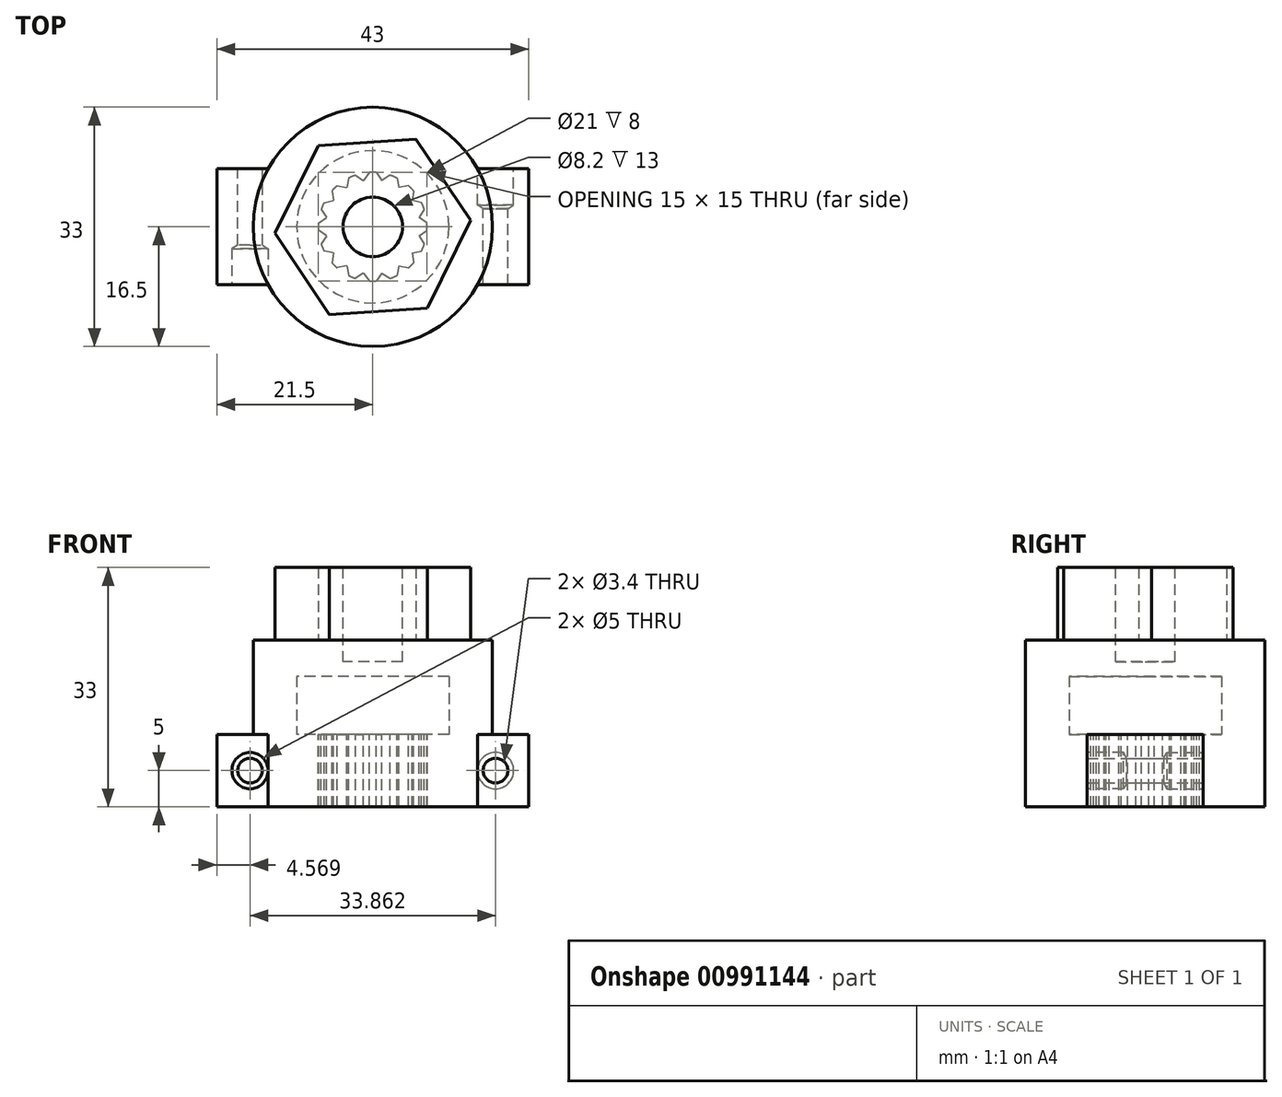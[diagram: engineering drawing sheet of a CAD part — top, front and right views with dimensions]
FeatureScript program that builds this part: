
annotation { "Feature Type Name" : "Feature", "Feature Type Description" : "" }
export const myFeature = defineFeature(function(context is Context, id is Id, definition is map)
    precondition{}
    {
        {
            var Q0;
            Q0=qCreatedBy(makeId("Top.planeOp"),FACE);
            var sketch = newSketch(context, id + "F0", { "sketchPlane" : qUnion([Q0])});
            skLineSegment(sketch, "E0", {"start": v(0, 0) * mm, "end": v(27.34, 0) * mm, "construction": true});
            skLineSegment(sketch, "E1", {"start": v(0, 0) * mm, "end": v(23.28, 9.64) * mm, "construction": true});
            skArc(sketch, "E2", {"start": v(7.5, 0) * mm, "mid": v(7.36, 1.46) * mm, "end": v(6.93, 2.87) * mm});
            skCircle(sketch, "E3", {"center": v(0, 0) * mm, "radius": 10.5 * mm});
            skLineSegment(sketch, "E4", {"start": v(7.5, 0) * mm, "end": v(10.5, 0) * mm});
            skLineSegment(sketch, "E5", {"start": v(10.5, 0) * mm, "end": v(21.5, 0) * mm});
            skLineSegment(sketch, "E6", {"start": v(21.5, 0) * mm, "end": v(21.5, 8) * mm});
            skLineSegment(sketch, "E7", {"start": v(21.5, 8) * mm, "end": v(14.43, 8) * mm});
            skLineSegment(sketch, "E8.MirrorCS", {"start": v(-10.5, 0) * mm, "end": v(-21.5, 0) * mm});
            skLineSegment(sketch, "E9.MirrorCS", {"start": v(-21.5, 0) * mm, "end": v(-21.5, 8) * mm});
            skLineSegment(sketch, "E10.MirrorCS", {"start": v(-21.5, 8) * mm, "end": v(-14.43, 8) * mm});
            skCircle(sketch, "E11", {"center": v(0, 0) * mm, "radius": 16.5 * mm});
            skLineSegment(sketch, "E12.MirrorCS", {"start": v(21.5, 0) * mm, "end": v(21.5, -8) * mm});
            skLineSegment(sketch, "E13.MirrorCS", {"start": v(21.5, -8) * mm, "end": v(14.43, -8) * mm});
            skLineSegment(sketch, "E14.MirrorCS", {"start": v(-21.5, 0) * mm, "end": v(-21.5, -8) * mm});
            skLineSegment(sketch, "E15.MirrorCS", {"start": v(-21.5, -8) * mm, "end": v(-14.43, -8) * mm});
            skLineSegment(sketch, "E16", {"start": v(-10.5, 0) * mm, "end": v(-7.5, 0) * mm});
            skLineSegment(sketch, "E17", {"start": v(7.36, 1.46) * mm, "end": v(0, 0) * mm, "construction": true});
            skLineSegment(sketch, "E18", {"start": v(7.1, 2.4) * mm, "end": v(6.38, 1.27) * mm});
            skLineSegment(sketch, "E19.MirrorCS", {"start": v(7.48, 0.5) * mm, "end": v(6.38, 1.27) * mm});
            skArc(sketch, "E20.1.0", {"start": v(6.93, 2.87) * mm, "mid": v(6.24, 4.17) * mm, "end": v(5.3, 5.3) * mm});
            skLineSegment(sketch, "E20.1.1", {"start": v(6.72, 3.33) * mm, "end": v(5.4, 3.61) * mm});
            skLineSegment(sketch, "E20.1.2", {"start": v(5.64, 4.94) * mm, "end": v(5.4, 3.61) * mm});
            skArc(sketch, "E20.2.0", {"start": v(5.3, 5.3) * mm, "mid": v(4.17, 6.24) * mm, "end": v(2.87, 6.93) * mm});
            skLineSegment(sketch, "E20.2.1", {"start": v(4.94, 5.64) * mm, "end": v(3.61, 5.4) * mm});
            skLineSegment(sketch, "E20.2.2", {"start": v(3.33, 6.72) * mm, "end": v(3.61, 5.4) * mm});
            skArc(sketch, "E21.2.3.0", {"start": v(2.87, 6.93) * mm, "mid": v(1.46, 7.36) * mm, "end": v(0, 7.5) * mm});
            skLineSegment(sketch, "E21.4.3.0", {"start": v(2.4, 7.1) * mm, "end": v(1.27, 6.38) * mm});
            skLineSegment(sketch, "E21.7.3.0", {"start": v(0.5, 7.48) * mm, "end": v(1.27, 6.38) * mm});
            skArc(sketch, "E21.2.4.0", {"start": v(0, 7.5) * mm, "mid": v(-1.46, 7.36) * mm, "end": v(-2.87, 6.93) * mm});
            skLineSegment(sketch, "E21.4.4.0", {"start": v(-0.5, 7.48) * mm, "end": v(-1.27, 6.38) * mm});
            skLineSegment(sketch, "E21.7.4.0", {"start": v(-2.4, 7.1) * mm, "end": v(-1.27, 6.38) * mm});
            skArc(sketch, "E21.2.5.0", {"start": v(-2.87, 6.93) * mm, "mid": v(-4.17, 6.24) * mm, "end": v(-5.3, 5.3) * mm});
            skLineSegment(sketch, "E21.4.5.0", {"start": v(-3.33, 6.72) * mm, "end": v(-3.61, 5.4) * mm});
            skLineSegment(sketch, "E21.7.5.0", {"start": v(-4.94, 5.64) * mm, "end": v(-3.61, 5.4) * mm});
            skArc(sketch, "E21.2.6.0", {"start": v(-5.3, 5.3) * mm, "mid": v(-6.24, 4.17) * mm, "end": v(-6.93, 2.87) * mm});
            skLineSegment(sketch, "E21.4.6.0", {"start": v(-5.64, 4.94) * mm, "end": v(-5.4, 3.61) * mm});
            skLineSegment(sketch, "E21.7.6.0", {"start": v(-6.72, 3.33) * mm, "end": v(-5.4, 3.61) * mm});
            skArc(sketch, "E21.2.7.0", {"start": v(-6.93, 2.87) * mm, "mid": v(-7.36, 1.46) * mm, "end": v(-7.5, 0) * mm});
            skLineSegment(sketch, "E21.4.7.0", {"start": v(-7.1, 2.4) * mm, "end": v(-6.38, 1.27) * mm});
            skLineSegment(sketch, "E21.7.7.0", {"start": v(-7.48, 0.5) * mm, "end": v(-6.38, 1.27) * mm});
            skArc(sketch, "E21.2.8.0", {"start": v(-7.5, 0) * mm, "mid": v(-7.36, -1.46) * mm, "end": v(-6.93, -2.87) * mm});
            skLineSegment(sketch, "E21.4.8.0", {"start": v(-7.48, -0.5) * mm, "end": v(-6.38, -1.27) * mm});
            skLineSegment(sketch, "E21.7.8.0", {"start": v(-7.1, -2.4) * mm, "end": v(-6.38, -1.27) * mm});
            skArc(sketch, "E21.2.9.0", {"start": v(-6.93, -2.87) * mm, "mid": v(-6.24, -4.17) * mm, "end": v(-5.3, -5.3) * mm});
            skLineSegment(sketch, "E21.4.9.0", {"start": v(-6.72, -3.33) * mm, "end": v(-5.4, -3.61) * mm});
            skLineSegment(sketch, "E21.7.9.0", {"start": v(-5.64, -4.94) * mm, "end": v(-5.4, -3.61) * mm});
            skArc(sketch, "E21.2.10.0", {"start": v(-5.3, -5.3) * mm, "mid": v(-4.17, -6.24) * mm, "end": v(-2.87, -6.93) * mm});
            skLineSegment(sketch, "E21.4.10.0", {"start": v(-4.94, -5.64) * mm, "end": v(-3.61, -5.4) * mm});
            skLineSegment(sketch, "E21.7.10.0", {"start": v(-3.33, -6.72) * mm, "end": v(-3.61, -5.4) * mm});
            skArc(sketch, "E21.2.11.0", {"start": v(-2.87, -6.93) * mm, "mid": v(-1.46, -7.36) * mm, "end": v(0, -7.5) * mm});
            skLineSegment(sketch, "E21.4.11.0", {"start": v(-2.4, -7.1) * mm, "end": v(-1.27, -6.38) * mm});
            skLineSegment(sketch, "E21.7.11.0", {"start": v(-0.5, -7.48) * mm, "end": v(-1.27, -6.38) * mm});
            skArc(sketch, "E21.2.12.0", {"start": v(0, -7.5) * mm, "mid": v(1.46, -7.36) * mm, "end": v(2.87, -6.93) * mm});
            skLineSegment(sketch, "E21.4.12.0", {"start": v(0.5, -7.48) * mm, "end": v(1.27, -6.38) * mm});
            skLineSegment(sketch, "E21.7.12.0", {"start": v(2.4, -7.1) * mm, "end": v(1.27, -6.38) * mm});
            skArc(sketch, "E21.2.13.0", {"start": v(2.87, -6.93) * mm, "mid": v(4.17, -6.24) * mm, "end": v(5.3, -5.3) * mm});
            skLineSegment(sketch, "E21.4.13.0", {"start": v(3.33, -6.72) * mm, "end": v(3.61, -5.4) * mm});
            skLineSegment(sketch, "E21.7.13.0", {"start": v(4.94, -5.64) * mm, "end": v(3.61, -5.4) * mm});
            skArc(sketch, "E21.2.14.0", {"start": v(5.3, -5.3) * mm, "mid": v(6.24, -4.17) * mm, "end": v(6.93, -2.87) * mm});
            skLineSegment(sketch, "E21.4.14.0", {"start": v(5.64, -4.94) * mm, "end": v(5.4, -3.61) * mm});
            skLineSegment(sketch, "E21.7.14.0", {"start": v(6.72, -3.33) * mm, "end": v(5.4, -3.61) * mm});
            skArc(sketch, "E21.2.15.0", {"start": v(6.93, -2.87) * mm, "mid": v(7.36, -1.46) * mm, "end": v(7.5, 0) * mm});
            skLineSegment(sketch, "E21.4.15.0", {"start": v(7.1, -2.4) * mm, "end": v(6.38, -1.27) * mm});
            skLineSegment(sketch, "E21.7.15.0", {"start": v(7.48, -0.5) * mm, "end": v(6.38, -1.27) * mm});
            skSolve(sketch);
        }
        {
            var Q0;
            {var subQ15=sQuery(id+"F0.wireOp",EDGE,"E4");Q0=makeQuery(id+"F0.imprint","IMPRINT",FACE,{"disambiguationData":[TD([[makeQuery(id+"F0.imprint","IMPRINT",EDGE,{"derivedFrom":subQ15}),1.0]])]});}
            var Q1;
            {var subQ0=sQuery(id+"F0.wireOp",EDGE,"e9f11277-7160-4ecf-99d4-2ce523c27c46.5.1");Q1=makeQuery(id+"F0.imprint","IMPRINT",FACE,{"disambiguationData":[TD([[makeQuery(id+"F0.imprint","IMPRINT",EDGE,{"derivedFrom":subQ0}),1.0]])]});}
            var Q2;
            {var subQ0=sQuery(id+"F0.wireOp",EDGE,"e9f11277-7160-4ecf-99d4-2ce523c27c46.4.1");Q2=makeQuery(id+"F0.imprint","IMPRINT",FACE,{"disambiguationData":[TD([[makeQuery(id+"F0.imprint","IMPRINT",EDGE,{"derivedFrom":subQ0}),1.0]])]});}
            var Q3;
            {var subQ0=sQuery(id+"F0.wireOp",EDGE,"e9f11277-7160-4ecf-99d4-2ce523c27c46.3.1");Q3=makeQuery(id+"F0.imprint","IMPRINT",FACE,{"disambiguationData":[TD([[makeQuery(id+"F0.imprint","IMPRINT",EDGE,{"derivedFrom":subQ0}),1.0]])]});}
            var Q4;
            {var subQ0=sQuery(id+"F0.wireOp",EDGE,"e9f11277-7160-4ecf-99d4-2ce523c27c46.2.1");Q4=makeQuery(id+"F0.imprint","IMPRINT",FACE,{"disambiguationData":[TD([[makeQuery(id+"F0.imprint","IMPRINT",EDGE,{"derivedFrom":subQ0}),1.0]])]});}
            var Q5;
            {var subQ0=sQuery(id+"F0.wireOp",EDGE,"e9f11277-7160-4ecf-99d4-2ce523c27c46.1.1");Q5=makeQuery(id+"F0.imprint","IMPRINT",FACE,{"disambiguationData":[TD([[makeQuery(id+"F0.imprint","IMPRINT",EDGE,{"derivedFrom":subQ0}),1.0]])]});}
            var Q6;
            {var subQ0=sQuery(id+"F0.wireOp",EDGE,"ZYJ7nTi2-fKZo-trrv-kjCt-nvlHvM4BSyAm");Q6=makeQuery(id+"F0.imprint","IMPRINT",FACE,{"disambiguationData":[TD([[makeQuery(id+"F0.imprint","IMPRINT",EDGE,{"derivedFrom":subQ0}),1.0]])]});}
            var Q7;
            {var subQ0=sQuery(id+"F0.wireOp",EDGE,"E5");Q7=makeQuery(id+"F0.imprint","IMPRINT",FACE,{"disambiguationData":[TD([[makeQuery(id+"F0.imprint","IMPRINT",EDGE,{"derivedFrom":subQ0}),1.0]])]});}
            var Q8;
            {var subQ0=sQuery(id+"F0.wireOp",EDGE,"E8.MirrorCS");Q8=makeQuery(id+"F0.imprint","IMPRINT",FACE,{"disambiguationData":[TD([[makeQuery(id+"F0.imprint","IMPRINT",EDGE,{"derivedFrom":subQ0}),-1.0]])]});}
            var Q9;
            {var subQ0=sQuery(id+"F0.wireOp",EDGE,"e9f11277-7160-4ecf-99d4-2ce523c27c46.6.1");Q9=makeQuery(id+"F0.imprint","IMPRINT",FACE,{"disambiguationData":[TD([[makeQuery(id+"F0.imprint","IMPRINT",EDGE,{"derivedFrom":subQ0}),1.0]])]});}
            var Q10;
            {var subQ0=sQuery(id+"F0.wireOp",EDGE,"E7");var subQ1=sQuery(id+"F0.wireOp",EDGE,"E3");var subQ2=makeQuery(id+"F0.imprint","INTERSECT",VERTEX,{"derivedFrom":[subQ1,subQ0]});Q10=makeQuery(id+"F0.imprint","IMPRINT",FACE,{"disambiguationData":[TD([[makeQuery(id+"F0.imprint","IMPRINT",EDGE,{"disambiguationData":[TD([[subQ2,-1.0]])],"derivedFrom":subQ1}),-1.0]])]});}
            var Q11;
            {var subQ0=sQuery(id+"F0.wireOp",EDGE,"E11");var subQ1=makeQuery(id+"F0.imprint","INTERSECT",VERTEX,{"derivedFrom":[sQuery(id+"F0.wireOp",EDGE,"E7"),subQ0]});Q11=makeQuery(id+"F0.imprint","IMPRINT",FACE,{"disambiguationData":[TD([[makeQuery(id+"F0.imprint","IMPRINT",EDGE,{"disambiguationData":[TD([[subQ1,1.0]])],"derivedFrom":subQ0}),1.0]])]});}
            var Q12;
            {var subQ0=sQuery(id+"F0.wireOp",EDGE,"e9f11277-7160-4ecf-99d4-2ce523c27c46.7.1");Q12=makeQuery(id+"F0.imprint","IMPRINT",FACE,{"disambiguationData":[TD([[makeQuery(id+"F0.imprint","IMPRINT",EDGE,{"derivedFrom":subQ0}),1.0]])]});}
            var Q13;
            {var subQ0=sQuery(id+"F0.wireOp",EDGE,"E21.4.7.0");Q13=makeQuery(id+"F0.imprint","IMPRINT",FACE,{"disambiguationData":[TD([[makeQuery(id+"F0.imprint","IMPRINT",EDGE,{"derivedFrom":subQ0}),-1.0]])]});}
            var Q14;
            {var subQ0=sQuery(id+"F0.wireOp",EDGE,"E21.4.6.0");Q14=makeQuery(id+"F0.imprint","IMPRINT",FACE,{"disambiguationData":[TD([[makeQuery(id+"F0.imprint","IMPRINT",EDGE,{"derivedFrom":subQ0}),-1.0]])]});}
            var Q15;
            {var subQ0=sQuery(id+"F0.wireOp",EDGE,"E21.4.5.0");Q15=makeQuery(id+"F0.imprint","IMPRINT",FACE,{"disambiguationData":[TD([[makeQuery(id+"F0.imprint","IMPRINT",EDGE,{"derivedFrom":subQ0}),-1.0]])]});}
            var Q16;
            {var subQ0=sQuery(id+"F0.wireOp",EDGE,"E21.4.4.0");Q16=makeQuery(id+"F0.imprint","IMPRINT",FACE,{"disambiguationData":[TD([[makeQuery(id+"F0.imprint","IMPRINT",EDGE,{"derivedFrom":subQ0}),-1.0]])]});}
            var Q17;
            {var subQ0=sQuery(id+"F0.wireOp",EDGE,"E21.4.3.0");Q17=makeQuery(id+"F0.imprint","IMPRINT",FACE,{"disambiguationData":[TD([[makeQuery(id+"F0.imprint","IMPRINT",EDGE,{"derivedFrom":subQ0}),-1.0]])]});}
            var Q18;
            {var subQ0=sQuery(id+"F0.wireOp",EDGE,"E20.2.1");Q18=makeQuery(id+"F0.imprint","IMPRINT",FACE,{"disambiguationData":[TD([[makeQuery(id+"F0.imprint","IMPRINT",EDGE,{"derivedFrom":subQ0}),-1.0]])]});}
            var Q19;
            {var subQ0=sQuery(id+"F0.wireOp",EDGE,"E20.1.1");Q19=makeQuery(id+"F0.imprint","IMPRINT",FACE,{"disambiguationData":[TD([[makeQuery(id+"F0.imprint","IMPRINT",EDGE,{"derivedFrom":subQ0}),-1.0]])]});}
            var Q20;
            {var subQ0=sQuery(id+"F0.wireOp",EDGE,"E18");Q20=makeQuery(id+"F0.imprint","IMPRINT",FACE,{"disambiguationData":[TD([[makeQuery(id+"F0.imprint","IMPRINT",EDGE,{"derivedFrom":subQ0}),1.0]])]});}
            extrude(context, id + "F1", {"entities" : qUnion([Q0, Q1, Q2, Q3, Q4, Q5, Q6, Q7, Q8, Q9, Q10, Q11, Q12, Q13, Q14, Q15, Q16, Q17, Q18, Q19, Q20]), "oppositeDirection" : true, "depth" : 10 * mm, "offsetDistance" : 25 * mm});
        }
        {
            var Q0;
            {var subQ0=sQuery(id+"F0.wireOp",EDGE,"e9f11277-7160-4ecf-99d4-2ce523c27c46.8.1");Q0=makeQuery(id+"F0.imprint","IMPRINT",FACE,{"disambiguationData":[TD([[makeQuery(id+"F0.imprint","IMPRINT",EDGE,{"derivedFrom":subQ0}),1.0]])]});}
            var Q1;
            {var subQ0=sQuery(id+"F0.wireOp",EDGE,"e9f11277-7160-4ecf-99d4-2ce523c27c46.9.1");Q1=makeQuery(id+"F0.imprint","IMPRINT",FACE,{"disambiguationData":[TD([[makeQuery(id+"F0.imprint","IMPRINT",EDGE,{"derivedFrom":subQ0}),1.0]])]});}
            var Q2;
            {var subQ0=sQuery(id+"F0.wireOp",EDGE,"e9f11277-7160-4ecf-99d4-2ce523c27c46.10.1");Q2=makeQuery(id+"F0.imprint","IMPRINT",FACE,{"disambiguationData":[TD([[makeQuery(id+"F0.imprint","IMPRINT",EDGE,{"derivedFrom":subQ0}),1.0]])]});}
            var Q3;
            {var subQ0=sQuery(id+"F0.wireOp",EDGE,"e9f11277-7160-4ecf-99d4-2ce523c27c46.11.1");Q3=makeQuery(id+"F0.imprint","IMPRINT",FACE,{"disambiguationData":[TD([[makeQuery(id+"F0.imprint","IMPRINT",EDGE,{"derivedFrom":subQ0}),1.0]])]});}
            var Q4;
            {var subQ0=sQuery(id+"F0.wireOp",EDGE,"e9f11277-7160-4ecf-99d4-2ce523c27c46.12.1");Q4=makeQuery(id+"F0.imprint","IMPRINT",FACE,{"disambiguationData":[TD([[makeQuery(id+"F0.imprint","IMPRINT",EDGE,{"derivedFrom":subQ0}),1.0]])]});}
            var Q5;
            {var subQ0=sQuery(id+"F0.wireOp",EDGE,"e9f11277-7160-4ecf-99d4-2ce523c27c46.13.1");Q5=makeQuery(id+"F0.imprint","IMPRINT",FACE,{"disambiguationData":[TD([[makeQuery(id+"F0.imprint","IMPRINT",EDGE,{"derivedFrom":subQ0}),1.0]])]});}
            var Q6;
            {var subQ0=sQuery(id+"F0.wireOp",EDGE,"e9f11277-7160-4ecf-99d4-2ce523c27c46.14.1");Q6=makeQuery(id+"F0.imprint","IMPRINT",FACE,{"disambiguationData":[TD([[makeQuery(id+"F0.imprint","IMPRINT",EDGE,{"derivedFrom":subQ0}),1.0]])]});}
            var Q7;
            {var subQ39=sQuery(id+"F0.wireOp",EDGE,"E4");Q7=makeQuery(id+"F0.imprint","IMPRINT",FACE,{"disambiguationData":[TD([[makeQuery(id+"F0.imprint","IMPRINT",EDGE,{"derivedFrom":subQ39}),-1.0]])]});}
            var Q8;
            {var subQ0=sQuery(id+"F0.wireOp",EDGE,"E5");var subQ5=sQuery(id+"F0.wireOp",EDGE,"E11");var subQ6=makeQuery(id+"F0.imprint","INTERSECT",VERTEX,{"derivedFrom":[subQ0,subQ5]});Q8=makeQuery(id+"F0.imprint","IMPRINT",FACE,{"disambiguationData":[TD([[makeQuery(id+"F0.imprint","IMPRINT",EDGE,{"disambiguationData":[TD([[subQ6,1.0]])],"derivedFrom":subQ5}),1.0]])]});}
            var Q9;
            {var subQ0=sQuery(id+"F0.wireOp",EDGE,"E14.MirrorCS");Q9=makeQuery(id+"F0.imprint","IMPRINT",FACE,{"disambiguationData":[TD([[makeQuery(id+"F0.imprint","IMPRINT",EDGE,{"derivedFrom":subQ0}),1.0]])]});}
            var Q10;
            {var subQ0=sQuery(id+"F0.wireOp",EDGE,"E12.MirrorCS");Q10=makeQuery(id+"F0.imprint","IMPRINT",FACE,{"disambiguationData":[TD([[makeQuery(id+"F0.imprint","IMPRINT",EDGE,{"derivedFrom":subQ0}),-1.0]])]});}
            var Q11;
            {var subQ0=sQuery(id+"F0.wireOp",EDGE,"62f9c568-41dd-46ed-b2ea-1909cac931a9.4.15.0");Q11=makeQuery(id+"F0.imprint","IMPRINT",FACE,{"disambiguationData":[TD([[makeQuery(id+"F0.imprint","IMPRINT",EDGE,{"derivedFrom":subQ0}),1.0]])]});}
            var Q12;
            {var subQ0=sQuery(id+"F0.wireOp",EDGE,"E21.4.8.0");Q12=makeQuery(id+"F0.imprint","IMPRINT",FACE,{"disambiguationData":[TD([[makeQuery(id+"F0.imprint","IMPRINT",EDGE,{"derivedFrom":subQ0}),-1.0]])]});}
            var Q13;
            {var subQ0=sQuery(id+"F0.wireOp",EDGE,"E21.4.9.0");Q13=makeQuery(id+"F0.imprint","IMPRINT",FACE,{"disambiguationData":[TD([[makeQuery(id+"F0.imprint","IMPRINT",EDGE,{"derivedFrom":subQ0}),-1.0]])]});}
            var Q14;
            {var subQ0=sQuery(id+"F0.wireOp",EDGE,"E21.4.10.0");Q14=makeQuery(id+"F0.imprint","IMPRINT",FACE,{"disambiguationData":[TD([[makeQuery(id+"F0.imprint","IMPRINT",EDGE,{"derivedFrom":subQ0}),-1.0]])]});}
            var Q15;
            {var subQ0=sQuery(id+"F0.wireOp",EDGE,"E21.4.11.0");Q15=makeQuery(id+"F0.imprint","IMPRINT",FACE,{"disambiguationData":[TD([[makeQuery(id+"F0.imprint","IMPRINT",EDGE,{"derivedFrom":subQ0}),-1.0]])]});}
            var Q16;
            {var subQ0=sQuery(id+"F0.wireOp",EDGE,"E21.4.12.0");Q16=makeQuery(id+"F0.imprint","IMPRINT",FACE,{"disambiguationData":[TD([[makeQuery(id+"F0.imprint","IMPRINT",EDGE,{"derivedFrom":subQ0}),-1.0]])]});}
            var Q17;
            {var subQ0=sQuery(id+"F0.wireOp",EDGE,"E21.4.13.0");Q17=makeQuery(id+"F0.imprint","IMPRINT",FACE,{"disambiguationData":[TD([[makeQuery(id+"F0.imprint","IMPRINT",EDGE,{"derivedFrom":subQ0}),-1.0]])]});}
            var Q18;
            {var subQ0=sQuery(id+"F0.wireOp",EDGE,"E21.4.14.0");Q18=makeQuery(id+"F0.imprint","IMPRINT",FACE,{"disambiguationData":[TD([[makeQuery(id+"F0.imprint","IMPRINT",EDGE,{"derivedFrom":subQ0}),-1.0]])]});}
            var Q19;
            {var subQ0=sQuery(id+"F0.wireOp",EDGE,"E21.4.15.0");Q19=makeQuery(id+"F0.imprint","IMPRINT",FACE,{"disambiguationData":[TD([[makeQuery(id+"F0.imprint","IMPRINT",EDGE,{"derivedFrom":subQ0}),-1.0]])]});}
            var Q20;
            Q20=makeQuery(id+"F1.opExtrude","CAP_FACE",FACE,{"disambiguationData":[OSD([sQuery(id+"F0.wireOp",EDGE,"E2"),sQuery(id+"F0.wireOp",EDGE,"ZYJ7nTi2-fKZo-trrv-kjCt-nvlHvM4BSyAm"),sQuery(id+"F0.wireOp",EDGE,"e9f11277-7160-4ecf-99d4-2ce523c27c46.1.0"),sQuery(id+"F0.wireOp",EDGE,"e9f11277-7160-4ecf-99d4-2ce523c27c46.1.1"),sQuery(id+"F0.wireOp",EDGE,"e9f11277-7160-4ecf-99d4-2ce523c27c46.2.0"),sQuery(id+"F0.wireOp",EDGE,"e9f11277-7160-4ecf-99d4-2ce523c27c46.2.1"),sQuery(id+"F0.wireOp",EDGE,"e9f11277-7160-4ecf-99d4-2ce523c27c46.3.0"),sQuery(id+"F0.wireOp",EDGE,"e9f11277-7160-4ecf-99d4-2ce523c27c46.3.1"),sQuery(id+"F0.wireOp",EDGE,"e9f11277-7160-4ecf-99d4-2ce523c27c46.4.0"),sQuery(id+"F0.wireOp",EDGE,"e9f11277-7160-4ecf-99d4-2ce523c27c46.4.1"),sQuery(id+"F0.wireOp",EDGE,"e9f11277-7160-4ecf-99d4-2ce523c27c46.5.0"),sQuery(id+"F0.wireOp",EDGE,"e9f11277-7160-4ecf-99d4-2ce523c27c46.5.1"),sQuery(id+"F0.wireOp",EDGE,"e9f11277-7160-4ecf-99d4-2ce523c27c46.6.0"),sQuery(id+"F0.wireOp",EDGE,"e9f11277-7160-4ecf-99d4-2ce523c27c46.6.1"),sQuery(id+"F0.wireOp",EDGE,"e9f11277-7160-4ecf-99d4-2ce523c27c46.7.0"),sQuery(id+"F0.wireOp",EDGE,"E4"),sQuery(id+"F0.wireOp",EDGE,"kGq2WO8g-F2tJ-uHDv-NIQt-d55ey2JGKq2Y"),sQuery(id+"F0.wireOp",EDGE,"E5"),sQuery(id+"F0.wireOp",EDGE,"E6"),sQuery(id+"F0.wireOp",EDGE,"E7"),sQuery(id+"F0.wireOp",EDGE,"E8.MirrorCS"),sQuery(id+"F0.wireOp",EDGE,"E9.MirrorCS"),sQuery(id+"F0.wireOp",EDGE,"E10.MirrorCS"),sQuery(id+"F0.wireOp",EDGE,"E11")])],"isStart":false});
            extrude(context, id + "F2", {"entities" : qUnion([Q0, Q1, Q2, Q3, Q4, Q5, Q6, Q7, Q8, Q9, Q10, Q11, Q12, Q13, Q14, Q15, Q16, Q17, Q18, Q19]), "endBound" : BoundingType.UP_TO_SURFACE, "oppositeDirection" : true, "depth" : 25 * mm, "endBoundEntityFace" : qUnion([Q20]), "offsetDistance" : 25 * mm});
        }
        {
            var Q0;
            {var subQ0=sQuery(id+"F0.wireOp",EDGE,"E11");var subQ1=makeQuery(id+"F0.imprint","INTERSECT",VERTEX,{"derivedFrom":[subQ0,sQuery(id+"F0.wireOp",EDGE,"E15.MirrorCS")]});Q0=makeQuery(id+"F0.imprint","IMPRINT",FACE,{"disambiguationData":[TD([[makeQuery(id+"F0.imprint","IMPRINT",EDGE,{"disambiguationData":[TD([[subQ1,1.0]])],"derivedFrom":subQ0}),1.0]])]});}
            var Q1;
            {var subQ0=sQuery(id+"F0.wireOp",EDGE,"E11");var subQ1=makeQuery(id+"F0.imprint","INTERSECT",VERTEX,{"derivedFrom":[sQuery(id+"F0.wireOp",EDGE,"E7"),subQ0]});Q1=makeQuery(id+"F0.imprint","IMPRINT",FACE,{"disambiguationData":[TD([[makeQuery(id+"F0.imprint","IMPRINT",EDGE,{"disambiguationData":[TD([[subQ1,1.0]])],"derivedFrom":subQ0}),1.0]])]});}
            extrude(context, id + "F3", {"entities" : qUnion([Q0, Q1]), "operationType" : NewBodyOperationType.ADD, "depth" : 8 * mm, "offsetDistance" : 25 * mm});
        }
        {
            var Q0;
            Q0=makeQuery(id+"F1.opExtrude","SWEPT_FACE",FACE,{"disambiguationData":[OSD([sQuery(id+"F0.wireOp",EDGE,"E7")])]});
            var sketch = newSketch(context, id + "F4", { "sketchPlane" : qUnion([Q0])});
            skPoint(sketch, "E22", {"position": v(-16.93, -5) * mm});
            skPoint(sketch, "E22.positionSnap0", {"position": v(-14.43, -5) * mm});
            skPoint(sketch, "E23.MirrorP", {"position": v(16.93, -5) * mm});
            skSolve(sketch);
        }
        {
            var Q0;
            Q0=sQuery(id+"F4.wireOp",VERTEX,"E22");
            var Q1;
            Q1=sQuery(id+"F4.wireOp",VERTEX,"E23.MirrorP");
            var Q2;
            Q2=makeQuery(id+"F1.opExtrude","SWEPT_BODY",BODY,{"disambiguationData":[OSD([sQuery(id+"F0.wireOp",EDGE,"E2"),sQuery(id+"F0.wireOp",EDGE,"E4"),sQuery(id+"F0.wireOp",EDGE,"E5"),sQuery(id+"F0.wireOp",EDGE,"E6"),sQuery(id+"F0.wireOp",EDGE,"E7"),sQuery(id+"F0.wireOp",EDGE,"E8.MirrorCS"),sQuery(id+"F0.wireOp",EDGE,"E9.MirrorCS"),sQuery(id+"F0.wireOp",EDGE,"E10.MirrorCS"),sQuery(id+"F0.wireOp",EDGE,"E11"),sQuery(id+"F0.wireOp",EDGE,"E16"),sQuery(id+"F0.wireOp",EDGE,"E18"),sQuery(id+"F0.wireOp",EDGE,"E19.MirrorCS"),sQuery(id+"F0.wireOp",EDGE,"E20.1.0"),sQuery(id+"F0.wireOp",EDGE,"E20.1.1"),sQuery(id+"F0.wireOp",EDGE,"E20.1.2"),sQuery(id+"F0.wireOp",EDGE,"E20.2.0"),sQuery(id+"F0.wireOp",EDGE,"E20.2.1"),sQuery(id+"F0.wireOp",EDGE,"E20.2.2"),sQuery(id+"F0.wireOp",EDGE,"E21.2.3.0"),sQuery(id+"F0.wireOp",EDGE,"E21.4.3.0"),sQuery(id+"F0.wireOp",EDGE,"E21.7.3.0"),sQuery(id+"F0.wireOp",EDGE,"E21.2.4.0"),sQuery(id+"F0.wireOp",EDGE,"E21.4.4.0"),sQuery(id+"F0.wireOp",EDGE,"E21.7.4.0"),sQuery(id+"F0.wireOp",EDGE,"E21.2.5.0"),sQuery(id+"F0.wireOp",EDGE,"E21.4.5.0"),sQuery(id+"F0.wireOp",EDGE,"E21.7.5.0"),sQuery(id+"F0.wireOp",EDGE,"E21.2.6.0"),sQuery(id+"F0.wireOp",EDGE,"E21.4.6.0"),sQuery(id+"F0.wireOp",EDGE,"E21.7.6.0"),sQuery(id+"F0.wireOp",EDGE,"E21.2.7.0"),sQuery(id+"F0.wireOp",EDGE,"E21.4.7.0"),sQuery(id+"F0.wireOp",EDGE,"E21.7.7.0")])]});
            var Q3;
            Q3=makeQuery(id+"F2.opExtrude","SWEPT_BODY",BODY,{"disambiguationData":[OSD([sQuery(id+"F0.wireOp",EDGE,"E4"),sQuery(id+"F0.wireOp",EDGE,"E5"),sQuery(id+"F0.wireOp",EDGE,"E8.MirrorCS"),sQuery(id+"F0.wireOp",EDGE,"E11"),sQuery(id+"F0.wireOp",EDGE,"E12.MirrorCS"),sQuery(id+"F0.wireOp",EDGE,"E13.MirrorCS"),sQuery(id+"F0.wireOp",EDGE,"E14.MirrorCS"),sQuery(id+"F0.wireOp",EDGE,"E15.MirrorCS"),sQuery(id+"F0.wireOp",EDGE,"E16"),sQuery(id+"F0.wireOp",EDGE,"E21.2.8.0"),sQuery(id+"F0.wireOp",EDGE,"E21.4.8.0"),sQuery(id+"F0.wireOp",EDGE,"E21.7.8.0"),sQuery(id+"F0.wireOp",EDGE,"E21.2.9.0"),sQuery(id+"F0.wireOp",EDGE,"E21.4.9.0"),sQuery(id+"F0.wireOp",EDGE,"E21.7.9.0"),sQuery(id+"F0.wireOp",EDGE,"E21.2.10.0"),sQuery(id+"F0.wireOp",EDGE,"E21.4.10.0"),sQuery(id+"F0.wireOp",EDGE,"E21.7.10.0"),sQuery(id+"F0.wireOp",EDGE,"E21.2.11.0"),sQuery(id+"F0.wireOp",EDGE,"E21.4.11.0"),sQuery(id+"F0.wireOp",EDGE,"E21.7.11.0"),sQuery(id+"F0.wireOp",EDGE,"E21.2.12.0"),sQuery(id+"F0.wireOp",EDGE,"E21.4.12.0"),sQuery(id+"F0.wireOp",EDGE,"E21.7.12.0"),sQuery(id+"F0.wireOp",EDGE,"E21.2.13.0"),sQuery(id+"F0.wireOp",EDGE,"E21.4.13.0"),sQuery(id+"F0.wireOp",EDGE,"E21.7.13.0"),sQuery(id+"F0.wireOp",EDGE,"E21.2.14.0"),sQuery(id+"F0.wireOp",EDGE,"E21.4.14.0"),sQuery(id+"F0.wireOp",EDGE,"E21.7.14.0"),sQuery(id+"F0.wireOp",EDGE,"E21.2.15.0"),sQuery(id+"F0.wireOp",EDGE,"E21.4.15.0"),sQuery(id+"F0.wireOp",EDGE,"E21.7.15.0")])]});
            hole(context, id + "F5", {"style" : HoleStyle.SIMPLE, "endStyle" : HoleEndStyle.THROUGH, "standardTappedOrClearance" : lookupTablePath({ "fit" : "Normal", "standard" : "ISO", "size" : "M3", "type" : "Clearance" }), "standardBlindInLast" : lookupTablePath({ "fit" : "Normal", "standard" : "ISO", "engagement" : "75%", "pitch" : "0.5 mm", "size" : "M3", "type" : "Clearance & tapped" }), "holeDiameter" : 3.4 * mm, "majorDiameter" : 5 * mm, "isTappedThrough" : true, "tappedDepth" : 12 * mm, "tapClearance" : 3, "locations" : qUnion([Q0, Q1]), "scope" : qUnion([Q2, Q3])});
        }
        {
            var Q0;
            Q0=makeQuery(id+"F2.opExtrude","SWEPT_FACE",FACE,{"disambiguationData":[OSD([sQuery(id+"F0.wireOp",EDGE,"E15.MirrorCS")])]});
            var sketch = newSketch(context, id + "F6", { "sketchPlane" : qUnion([Q0])});
            skPoint(sketch, "E24", {"position": v(-16.93, -5) * mm});
            skSolve(sketch);
        }
        {
            var Q0;
            Q0=sQuery(id+"F4.wireOp",VERTEX,"E22");
            var Q1;
            Q1=sQuery(id+"F6.wireOp",VERTEX,"E24");
            var Q2;
            Q2=makeQuery(id+"F1.opExtrude","SWEPT_BODY",BODY,{"disambiguationData":[OSD([sQuery(id+"F0.wireOp",EDGE,"E2"),sQuery(id+"F0.wireOp",EDGE,"E4"),sQuery(id+"F0.wireOp",EDGE,"E5"),sQuery(id+"F0.wireOp",EDGE,"E6"),sQuery(id+"F0.wireOp",EDGE,"E7"),sQuery(id+"F0.wireOp",EDGE,"E8.MirrorCS"),sQuery(id+"F0.wireOp",EDGE,"E9.MirrorCS"),sQuery(id+"F0.wireOp",EDGE,"E10.MirrorCS"),sQuery(id+"F0.wireOp",EDGE,"E11"),sQuery(id+"F0.wireOp",EDGE,"E16"),sQuery(id+"F0.wireOp",EDGE,"E18"),sQuery(id+"F0.wireOp",EDGE,"E19.MirrorCS"),sQuery(id+"F0.wireOp",EDGE,"E20.1.0"),sQuery(id+"F0.wireOp",EDGE,"E20.1.1"),sQuery(id+"F0.wireOp",EDGE,"E20.1.2"),sQuery(id+"F0.wireOp",EDGE,"E20.2.0"),sQuery(id+"F0.wireOp",EDGE,"E20.2.1"),sQuery(id+"F0.wireOp",EDGE,"E20.2.2"),sQuery(id+"F0.wireOp",EDGE,"E21.2.3.0"),sQuery(id+"F0.wireOp",EDGE,"E21.4.3.0"),sQuery(id+"F0.wireOp",EDGE,"E21.7.3.0"),sQuery(id+"F0.wireOp",EDGE,"E21.2.4.0"),sQuery(id+"F0.wireOp",EDGE,"E21.4.4.0"),sQuery(id+"F0.wireOp",EDGE,"E21.7.4.0"),sQuery(id+"F0.wireOp",EDGE,"E21.2.5.0"),sQuery(id+"F0.wireOp",EDGE,"E21.4.5.0"),sQuery(id+"F0.wireOp",EDGE,"E21.7.5.0"),sQuery(id+"F0.wireOp",EDGE,"E21.2.6.0"),sQuery(id+"F0.wireOp",EDGE,"E21.4.6.0"),sQuery(id+"F0.wireOp",EDGE,"E21.7.6.0"),sQuery(id+"F0.wireOp",EDGE,"E21.2.7.0"),sQuery(id+"F0.wireOp",EDGE,"E21.4.7.0"),sQuery(id+"F0.wireOp",EDGE,"E21.7.7.0")])]});
            var Q3;
            Q3=makeQuery(id+"F2.opExtrude","SWEPT_BODY",BODY,{"disambiguationData":[OSD([sQuery(id+"F0.wireOp",EDGE,"E4"),sQuery(id+"F0.wireOp",EDGE,"E5"),sQuery(id+"F0.wireOp",EDGE,"E8.MirrorCS"),sQuery(id+"F0.wireOp",EDGE,"E11"),sQuery(id+"F0.wireOp",EDGE,"E12.MirrorCS"),sQuery(id+"F0.wireOp",EDGE,"E13.MirrorCS"),sQuery(id+"F0.wireOp",EDGE,"E14.MirrorCS"),sQuery(id+"F0.wireOp",EDGE,"E15.MirrorCS"),sQuery(id+"F0.wireOp",EDGE,"E16"),sQuery(id+"F0.wireOp",EDGE,"E21.2.8.0"),sQuery(id+"F0.wireOp",EDGE,"E21.4.8.0"),sQuery(id+"F0.wireOp",EDGE,"E21.7.8.0"),sQuery(id+"F0.wireOp",EDGE,"E21.2.9.0"),sQuery(id+"F0.wireOp",EDGE,"E21.4.9.0"),sQuery(id+"F0.wireOp",EDGE,"E21.7.9.0"),sQuery(id+"F0.wireOp",EDGE,"E21.2.10.0"),sQuery(id+"F0.wireOp",EDGE,"E21.4.10.0"),sQuery(id+"F0.wireOp",EDGE,"E21.7.10.0"),sQuery(id+"F0.wireOp",EDGE,"E21.2.11.0"),sQuery(id+"F0.wireOp",EDGE,"E21.4.11.0"),sQuery(id+"F0.wireOp",EDGE,"E21.7.11.0"),sQuery(id+"F0.wireOp",EDGE,"E21.2.12.0"),sQuery(id+"F0.wireOp",EDGE,"E21.4.12.0"),sQuery(id+"F0.wireOp",EDGE,"E21.7.12.0"),sQuery(id+"F0.wireOp",EDGE,"E21.2.13.0"),sQuery(id+"F0.wireOp",EDGE,"E21.4.13.0"),sQuery(id+"F0.wireOp",EDGE,"E21.7.13.0"),sQuery(id+"F0.wireOp",EDGE,"E21.2.14.0"),sQuery(id+"F0.wireOp",EDGE,"E21.4.14.0"),sQuery(id+"F0.wireOp",EDGE,"E21.7.14.0"),sQuery(id+"F0.wireOp",EDGE,"E21.2.15.0"),sQuery(id+"F0.wireOp",EDGE,"E21.4.15.0"),sQuery(id+"F0.wireOp",EDGE,"E21.7.15.0")])]});
            hole(context, id + "F7", {"style" : HoleStyle.SIMPLE, "endStyle" : HoleEndStyle.BLIND, "holeDiameter" : 5 * mm, "majorDiameter" : 5 * mm, "holeDepth" : 5 * mm, "isTappedThrough" : true, "tappedDepth" : 12 * mm, "tapClearance" : 3, "locations" : qUnion([Q0, Q1]), "scope" : qUnion([Q2, Q3])});
        }
        {
            var Q0;
            Q0=makeQuery(id+"F3.opExtrude","CAP_FACE",FACE,{"disambiguationData":[OSD([sQuery(id+"F0.wireOp",EDGE,"E3"),sQuery(id+"F0.wireOp",EDGE,"E11")])],"isStart":false});
            var sketch = newSketch(context, id + "F8", { "sketchPlane" : qUnion([Q0])});
            skCircle(sketch, "E25.0", {"center": v(0, 0) * mm, "radius": 16.5 * mm});
            skSolve(sketch);
        }
        {
            var Q0;
            Q0=makeQuery(id+"F8.imprint","IMPRINT",FACE,{"disambiguationData":[TD([[makeQuery(id+"F8.imprint","IMPRINT",EDGE,{"derivedFrom":sQuery(id+"F8.wireOp",EDGE,"E25.0")}),1.0]])]});
            var Q1;
            Q1=makeQuery(id+"F8.imprint","IMPRINT",FACE,{"disambiguationData":[TD([[makeQuery(id+"F8.imprint","IMPRINT",EDGE,{"derivedFrom":makeQuery(id+"F3.opExtrude","CAP_EDGE",EDGE,{"disambiguationData":[OSD([sQuery(id+"F0.wireOp",EDGE,"E3")])],"isStart":false})}),1.0]])]});
            extrude(context, id + "F9", {"entities" : qUnion([Q0, Q1]), "operationType" : NewBodyOperationType.ADD, "depth" : 5 * mm, "offsetDistance" : 25 * mm});
        }
        {
            var Q0;
            Q0=makeQuery(id+"F9.opExtrude","CAP_FACE",FACE,{"disambiguationData":[OSD([sQuery(id+"F8.wireOp",EDGE,"E25.0")])],"isStart":false});
            var sketch = newSketch(context, id + "F10", { "sketchPlane" : qUnion([Q0])});
            skCircle(sketch, "E26.cCircle", {"center": v(0, 0) * mm, "radius": 11.7 * mm, "construction": true});
            skLineSegment(sketch, "E26.0", {"start": v(-13.47, -0.88) * mm, "end": v(-7.5, 11.22) * mm});
            skLineSegment(sketch, "E26.1", {"start": v(-7.5, 11.22) * mm, "end": v(5.97, 12.1) * mm});
            skLineSegment(sketch, "E26.2", {"start": v(5.97, 12.1) * mm, "end": v(13.47, 0.88) * mm});
            skLineSegment(sketch, "E26.3", {"start": v(13.47, 0.88) * mm, "end": v(7.5, -11.22) * mm});
            skLineSegment(sketch, "E26.4", {"start": v(7.5, -11.22) * mm, "end": v(-5.97, -12.1) * mm});
            skLineSegment(sketch, "E26.5", {"start": v(-5.97, -12.1) * mm, "end": v(-13.47, -0.88) * mm});
            skPoint(sketch, "E26.0.midPoint", {"position": v(-10.49, 5.17) * mm});
            skSolve(sketch);
        }
        {
            var Q0;
            Q0=makeQuery(id+"F10.imprint","IMPRINT",FACE,{"disambiguationData":[TD([[makeQuery(id+"F10.imprint","IMPRINT",EDGE,{"derivedFrom":sQuery(id+"F10.wireOp",EDGE,"E26.0")}),-1.0]])]});
            extrude(context, id + "F11", {"entities" : qUnion([Q0]), "operationType" : NewBodyOperationType.ADD, "depth" : 10 * mm, "offsetDistance" : 25 * mm});
        }
        {
            var Q0;
            Q0=makeQuery(id+"F11.opExtrude","CAP_FACE",FACE,{"disambiguationData":[OSD([sQuery(id+"F10.wireOp",EDGE,"E26.0"),sQuery(id+"F10.wireOp",EDGE,"E26.1"),sQuery(id+"F10.wireOp",EDGE,"E26.2"),sQuery(id+"F10.wireOp",EDGE,"E26.3"),sQuery(id+"F10.wireOp",EDGE,"E26.4"),sQuery(id+"F10.wireOp",EDGE,"E26.5")])],"isStart":false});
            var sketch = newSketch(context, id + "F12", { "sketchPlane" : qUnion([Q0])});
            skPoint(sketch, "E27.0", {"position": v(0, 0) * mm});
            skCircle(sketch, "E28", {"center": v(0, 0) * mm, "radius": 4.1 * mm});
            skSolve(sketch);
        }
        {
            var Q0;
            Q0=makeQuery(id+"F12.imprint","IMPRINT",FACE,{"disambiguationData":[TD([[makeQuery(id+"F12.imprint","IMPRINT",EDGE,{"derivedFrom":sQuery(id+"F12.wireOp",EDGE,"E28")}),1.0]])]});
            var Q1;
            Q1=makeQuery(id+"F9.opExtrude","CAP_FACE",FACE,{"disambiguationData":[OSD([sQuery(id+"F8.wireOp",EDGE,"E25.0")])],"isStart":true});
            extrude(context, id + "F13", {"entities" : qUnion([Q0]), "operationType" : NewBodyOperationType.REMOVE, "endBound" : BoundingType.UP_TO_SURFACE, "oppositeDirection" : true, "depth" : 25 * mm, "endBoundEntityFace" : qUnion([Q1]), "hasOffset" : true, "offsetDistance" : 2 * mm});
        }
    });
